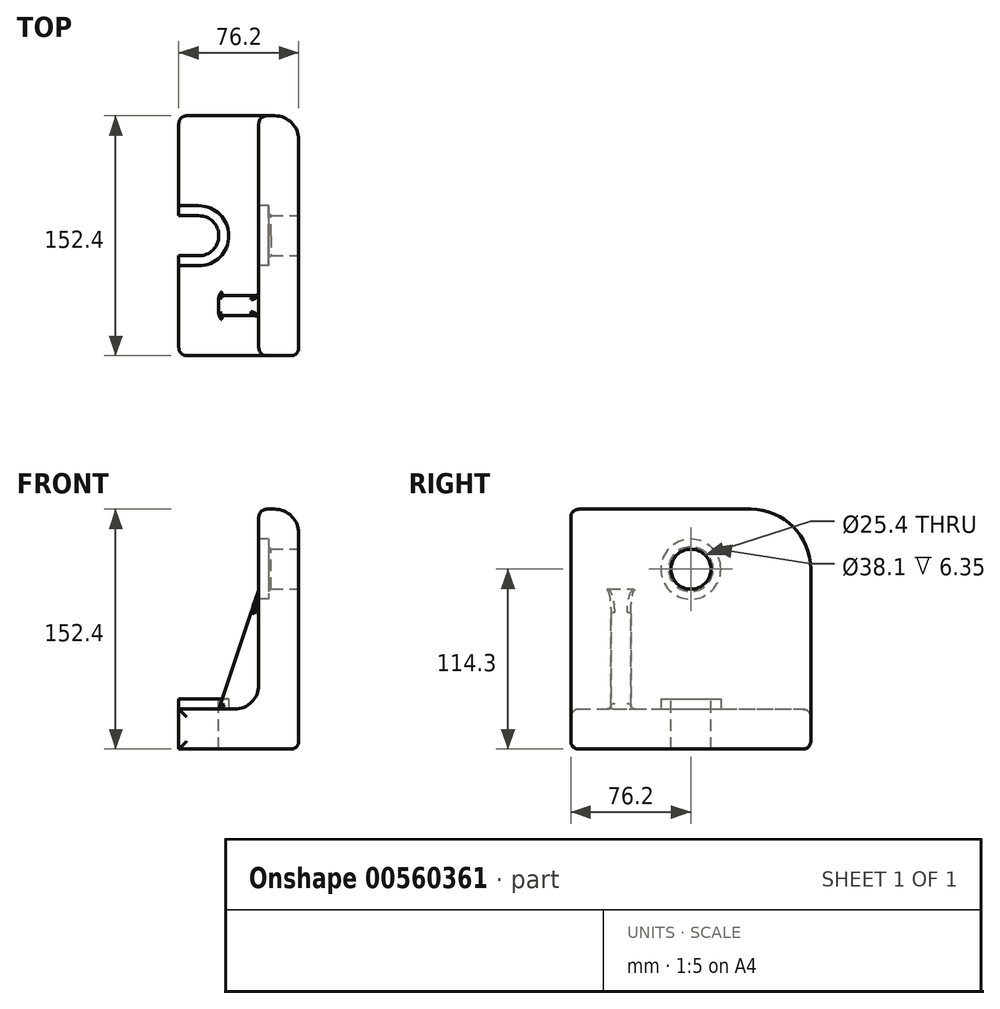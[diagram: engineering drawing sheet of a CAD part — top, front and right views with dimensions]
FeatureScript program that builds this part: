
annotation { "Feature Type Name" : "Feature", "Feature Type Description" : "" }
export const myFeature = defineFeature(function(context is Context, id is Id, definition is map)
    precondition{}
    {
        {
            var Q0;
            Q0=qCreatedBy(makeId("Front.planeOp"),FACE);
            var sketch = newSketch(context, id + "F0", { "sketchPlane" : qUnion([Q0])});
            skLineSegment(sketch, "E0.bottom", {"start": v(0, 0) * mm, "end": v(-76.2, 0) * mm});
            skLineSegment(sketch, "E0.top", {"start": v(-25.4, 25.4) * mm, "end": v(-76.2, 25.4) * mm});
            skLineSegment(sketch, "E0.left", {"start": v(0, 0) * mm, "end": v(0, 25.4) * mm});
            skLineSegment(sketch, "E0.right", {"start": v(-76.2, 0) * mm, "end": v(-76.2, 25.4) * mm});
            skLineSegment(sketch, "E1.bottom", {"start": v(0, 0) * mm, "end": v(-25.4, 0) * mm});
            skLineSegment(sketch, "E1.top", {"start": v(0, 152.4) * mm, "end": v(-25.4, 152.4) * mm});
            skLineSegment(sketch, "E1.left", {"start": v(0, 0) * mm, "end": v(0, 152.4) * mm});
            skLineSegment(sketch, "E1.right", {"start": v(-25.4, 25.4) * mm, "end": v(-25.4, 152.4) * mm});
            skSolve(sketch);
        }
        {
            var Q0;
            Q0 = qSketchRegion(id + "F0", true);
            extrude(context, id + "F1", {"entities" : qUnion([Q0]), "endBound" : BoundingType.SYMMETRIC, "depth" : 152.4 * mm, "offsetDistance" : 25.4 * mm});
        }
        {
            var Q0;
            Q0=makeQuery(id+"F1.opExtrude","SWEPT_FACE",FACE,{"disambiguationData":[OSD([sQuery(id+"F0.wireOp",EDGE,"E1.left")])]});
            var sketch = newSketch(context, id + "F2", { "sketchPlane" : qUnion([Q0])});
            skCircle(sketch, "E2", {"center": v(0, 114.3) * mm, "radius": 12.7 * mm});
            skSolve(sketch);
        }
        {
            var Q0;
            Q0=makeQuery(id+"F2.imprint","IMPRINT",FACE,{"disambiguationData":[TD([[makeQuery(id+"F2.imprint","IMPRINT",EDGE,{"derivedFrom":sQuery(id+"F2.wireOp",EDGE,"E2")}),1.0]])]});
            extrude(context, id + "F3", {"entities" : qUnion([Q0]), "operationType" : NewBodyOperationType.REMOVE, "endBound" : BoundingType.THROUGH_ALL, "oppositeDirection" : true, "depth" : 25.4 * mm, "offsetDistance" : 25.4 * mm});
        }
        {
            var Q0;
            Q0=makeQuery(id+"F1.opExtrude","SWEPT_FACE",FACE,{"disambiguationData":[OSD([sQuery(id+"F0.wireOp",EDGE,"E0.top")])]});
            var sketch = newSketch(context, id + "F4", { "sketchPlane" : qUnion([Q0])});
            skLineSegment(sketch, "E3", {"start": v(-76.2, 12.7) * mm, "end": v(-63.5, 12.7) * mm});
            skArc(sketch, "E4", {"start": v(-63.5, 12.7) * mm, "mid": v(-50.8, 0) * mm, "end": v(-63.5, -12.7) * mm});
            skLineSegment(sketch, "E5", {"start": v(-63.5, -12.7) * mm, "end": v(-76.2, -12.7) * mm});
            skLineSegment(sketch, "E6", {"start": v(-76.2, -12.7) * mm, "end": v(-76.2, 12.7) * mm});
            skSolve(sketch);
        }
        {
            var Q0;
            Q0 = qSketchRegion(id + "F4", true);
            extrude(context, id + "F5", {"entities" : qUnion([Q0]), "operationType" : NewBodyOperationType.REMOVE, "endBound" : BoundingType.THROUGH_ALL, "oppositeDirection" : true, "depth" : 25.4 * mm, "offsetDistance" : 25.4 * mm});
        }
        {
            var Q0;
            Q0=makeQuery(id+"F1.opExtrude","SWEPT_FACE",FACE,{"disambiguationData":[OSD([sQuery(id+"F0.wireOp",EDGE,"E1.right")])]});
            var sketch = newSketch(context, id + "F6", { "sketchPlane" : qUnion([Q0])});
            skLineSegment(sketch, "E7.0", {"start": v(-76.2, 25.4) * mm, "end": v(-76.2, 152.4) * mm});
            skLineSegment(sketch, "E7.1", {"start": v(76.2, 152.4) * mm, "end": v(-76.2, 152.4) * mm});
            skArc(sketch, "E8", {"start": v(-38.1, 152.4) * mm, "mid": v(-65.04, 141.24) * mm, "end": v(-76.2, 114.3) * mm});
            skSolve(sketch);
        }
        {
            var Q0;
            {var subQ3=sQuery(id+"F6.wireOp",EDGE,"E8");Q0=makeQuery(id+"F6.imprint","IMPRINT",FACE,{"disambiguationData":[TD([[makeQuery(id+"F6.imprint","IMPRINT",EDGE,{"derivedFrom":subQ3}),-1.0]])]});}
            extrude(context, id + "F7", {"entities" : qUnion([Q0]), "operationType" : NewBodyOperationType.REMOVE, "endBound" : BoundingType.THROUGH_ALL, "oppositeDirection" : true, "depth" : 25.4 * mm, "offsetDistance" : 25.4 * mm});
        }
        {
            var Q0;
            Q0=makeQuery(id+"F1.opExtrude","SWEPT_FACE",FACE,{"disambiguationData":[OSD([sQuery(id+"F0.wireOp",EDGE,"E1.right")])]});
            var sketch = newSketch(context, id + "F8", { "sketchPlane" : qUnion([Q0])});
            skCircle(sketch, "E9", {"center": v(0, 114.3) * mm, "radius": 19.05 * mm});
            skSolve(sketch);
        }
        {
            var Q0;
            Q0=makeQuery(id+"F8.imprint","IMPRINT",FACE,{"disambiguationData":[TD([[makeQuery(id+"F8.imprint","IMPRINT",EDGE,{"derivedFrom":makeQuery(id+"F3.boolean.opBoolean","INTERSECT",EDGE,{"derivedFrom":[makeQuery(id+"F1.opExtrude","SWEPT_FACE",FACE,{"disambiguationData":[OSD([sQuery(id+"F0.wireOp",EDGE,"E1.right")])]}),makeQuery(id+"F3.opExtrude","SWEPT_FACE",FACE,{"disambiguationData":[OSD([sQuery(id+"F2.wireOp",EDGE,"E2")])]})]})}),1.0]])]});
            var Q1;
            Q1=makeQuery(id+"F8.imprint","IMPRINT",FACE,{"disambiguationData":[TD([[makeQuery(id+"F8.imprint","IMPRINT",EDGE,{"derivedFrom":sQuery(id+"F8.wireOp",EDGE,"E9")}),1.0]])]});
            extrude(context, id + "F9", {"entities" : qUnion([Q0, Q1]), "operationType" : NewBodyOperationType.REMOVE, "oppositeDirection" : true, "depth" : 6.35 * mm, "offsetDistance" : 25.4 * mm});
        }
        {
            var Q0;
            Q0=qCreatedBy(makeId("Front.planeOp"),FACE);
            cPlane(context, id + "F10", {"entities" : qUnion([Q0]), "cplaneType" : CPlaneType.OFFSET, "offset" : 44.45 * mm, "width" : 152.4 * mm, "height" : 152.4 * mm});
        }
        {
            var Q0;
            Q0=qCreatedBy(id+"F10.planeOp",FACE);
            var sketch = newSketch(context, id + "F11", { "sketchPlane" : qUnion([Q0])});
            skLineSegment(sketch, "E10.0", {"start": v(-25.4, 25.4) * mm, "end": v(-76.2, 25.4) * mm});
            skLineSegment(sketch, "E10.1", {"start": v(-25.4, 25.4) * mm, "end": v(-25.4, 114.3) * mm});
            skLineSegment(sketch, "E11", {"start": v(-25.4, 101.6) * mm, "end": v(-50.8, 25.4) * mm});
            skLineSegment(sketch, "E12", {"start": v(-25.4, 101.6) * mm, "end": v(-25.4, 25.4) * mm});
            skLineSegment(sketch, "E13", {"start": v(-50.8, 25.4) * mm, "end": v(-25.4, 25.4) * mm});
            skLineSegment(sketch, "E14", {"start": v(-50.8, 25.4) * mm, "end": v(-76.2, 25.4) * mm});
            skSolve(sketch);
        }
        {
            var Q0;
            Q0=makeQuery(id+"F11.imprint","IMPRINT",FACE,{"disambiguationData":[TD([[makeQuery(id+"F11.imprint","IMPRINT",EDGE,{"derivedFrom":sQuery(id+"F11.wireOp",EDGE,"E11")}),1.0]])]});
            extrude(context, id + "F12", {"entities" : qUnion([Q0]), "operationType" : NewBodyOperationType.ADD, "endBound" : BoundingType.SYMMETRIC, "depth" : 12.7 * mm, "offsetDistance" : 25.4 * mm});
        }
        {
            var Q0;
            Q0=makeQuery(id+"F9.boolean.opBoolean","INTERSECT",EDGE,{"derivedFrom":[makeQuery(id+"F3.boolean.opBoolean","COPY",FACE,{"derivedFrom":makeQuery(id+"F3.opExtrude","SWEPT_FACE",FACE,{"disambiguationData":[OSD([sQuery(id+"F2.wireOp",EDGE,"E2")])]})}),makeQuery(id+"F9.opExtrude","CAP_FACE",FACE,{"disambiguationData":[OSD([sQuery(id+"F8.wireOp",EDGE,"E9")])],"isStart":false})]});
            var Q1;
            Q1=makeQuery(id+"F9.boolean.opBoolean","COPY",EDGE,{"derivedFrom":makeQuery(id+"F9.opExtrude","CAP_EDGE",EDGE,{"disambiguationData":[OSD([sQuery(id+"F8.wireOp",EDGE,"E9")])],"isStart":true})});
            chamfer(context, id + "F13", {"entities" : qUnion([Q0, Q1]), "width" : 1.52 * mm, "tangentPropagation" : true});
        }
        {
            var Q0;
            Q0=makeQuery(id+"F1.opExtrude","SWEPT_FACE",FACE,{"disambiguationData":[OSD([sQuery(id+"F0.wireOp",EDGE,"E0.top")])]});
            var sketch = newSketch(context, id + "F14", { "sketchPlane" : qUnion([Q0])});
            skLineSegment(sketch, "E15.0", {"start": v(-76.2, 12.7) * mm, "end": v(-76.2, 76.2) * mm});
            skLineSegment(sketch, "E15.1", {"start": v(-76.2, 12.7) * mm, "end": v(-63.5, 12.7) * mm});
            skArc(sketch, "E15.2", {"start": v(-63.5, 12.7) * mm, "mid": v(-50.8, 0) * mm, "end": v(-63.5, -12.7) * mm});
            skLineSegment(sketch, "E15.3", {"start": v(-63.5, -12.7) * mm, "end": v(-76.2, -12.7) * mm});
            skLineSegment(sketch, "E15.4", {"start": v(-76.2, -76.2) * mm, "end": v(-76.2, -12.7) * mm});
            skLineSegment(sketch, "E16.0", {"start": v(-76.2, 19.05) * mm, "end": v(-63.5, 19.05) * mm});
            skArc(sketch, "E17.0", {"start": v(-63.5, 19.05) * mm, "mid": v(-44.45, 0) * mm, "end": v(-63.5, -19.05) * mm});
            skLineSegment(sketch, "E18.0", {"start": v(-63.5, -19.05) * mm, "end": v(-76.2, -19.05) * mm});
            skSolve(sketch);
        }
        {
            var Q0;
            {var subQ1=sQuery(id+"F14.wireOp",EDGE,"E15.1");Q0=makeQuery(id+"F14.imprint","IMPRINT",FACE,{"disambiguationData":[TD([[makeQuery(id+"F14.imprint","IMPRINT",EDGE,{"derivedFrom":subQ1}),1.0]])]});}
            extrude(context, id + "F15", {"entities" : qUnion([Q0]), "operationType" : NewBodyOperationType.ADD, "depth" : 6.35 * mm, "offsetDistance" : 25.4 * mm});
        }
        {
            var Q0;
            Q0=makeQuery(id+"F1.opExtrude","SWEPT_EDGE",EDGE,{"disambiguationData":[OSD([sQuery(id+"F0.wireOp",EDGE,"E1.bottom"),sQuery(id+"F0.wireOp",EDGE,"E1.left")])]});
            var Q1;
            {var subQ0=sQuery(id+"F0.wireOp",EDGE,"E1.right");var subQ1=sQuery(id+"F0.wireOp",EDGE,"E0.top");var subQ5=sQuery(id+"F11.wireOp",EDGE,"E13");var subQ6=sQuery(id+"F11.wireOp",EDGE,"E12");var subQ7=sQuery(id+"F11.wireOp",EDGE,"E11");Q1=makeQuery(id+"FHcutw4A6m2gUYd_1.1.F12.boolean.opBoolean","SPLIT",EDGE,{"disambiguationData":[TD([makeQuery(id+"FHcutw4A6m2gUYd_1.1.F12.opExtrude","CAP_FACE",FACE,{"disambiguationData":[OSD([subQ7,subQ6,subQ5])],"isStart":false})])],"derivedFrom":makeQuery(id+"F12.boolean.opBoolean","SPLIT",EDGE,{"disambiguationData":[TD([makeQuery(id+"F12.opExtrude","CAP_FACE",FACE,{"disambiguationData":[OSD([subQ7,subQ6,subQ5])],"isStart":true})])],"derivedFrom":makeQuery(id+"F1.opExtrude","SWEPT_EDGE",EDGE,{"disambiguationData":[OSD([subQ1,subQ0])]})})});}
            var Q2;
            {var subQ0=sQuery(id+"F0.wireOp",EDGE,"E0.top");var subQ2=sQuery(id+"F0.wireOp",EDGE,"E1.right");var subQ4=sQuery(id+"F11.wireOp",EDGE,"E13");var subQ5=sQuery(id+"F11.wireOp",EDGE,"E12");var subQ6=sQuery(id+"F11.wireOp",EDGE,"E11");var subQ7=makeQuery(id+"F12.opExtrude","CAP_FACE",FACE,{"disambiguationData":[OSD([subQ6,subQ5,subQ4])],"isStart":true});Q2=makeQuery(id+"FHcutw4A6m2gUYd_1.1.F12.boolean.opBoolean","SPLIT",EDGE,{"disambiguationData":[TD([subQ7])],"derivedFrom":makeQuery(id+"F12.boolean.opBoolean","SPLIT",EDGE,{"disambiguationData":[TD([subQ7])],"derivedFrom":makeQuery(id+"F1.opExtrude","SWEPT_EDGE",EDGE,{"disambiguationData":[OSD([subQ0,subQ2])]})})});}
            var Q3;
            {var subQ0=sQuery(id+"F0.wireOp",EDGE,"E1.right");var subQ1=sQuery(id+"F0.wireOp",EDGE,"E0.top");Q3=makeQuery(id+"F12.boolean.opBoolean","SPLIT",EDGE,{"disambiguationData":[TD([makeQuery(id+"F12.opExtrude","CAP_FACE",FACE,{"disambiguationData":[OSD([sQuery(id+"F11.wireOp",EDGE,"E11"),sQuery(id+"F11.wireOp",EDGE,"E12"),sQuery(id+"F11.wireOp",EDGE,"E13")])],"isStart":false})])],"derivedFrom":makeQuery(id+"F1.opExtrude","SWEPT_EDGE",EDGE,{"disambiguationData":[OSD([subQ1,subQ0])]})});}
            fillet(context, id + "F16", {"entities" : qUnion([Q0, Q1, Q2, Q3]), "radius" : 15.24 * mm, "tangentPropagation" : true, "allowEdgeOverflow" : false});
        }
        {
            var Q0;
            Q0=makeQuery(id+"F1.opExtrude","CAP_EDGE",EDGE,{"disambiguationData":[OSD([sQuery(id+"F0.wireOp",EDGE,"E0.top")])],"isStart":false});
            var Q1;
            Q1=makeQuery(id+"F1.opExtrude","CAP_EDGE",EDGE,{"disambiguationData":[OSD([sQuery(id+"F0.wireOp",EDGE,"E1.right")])],"isStart":false});
            var Q2;
            Q2=makeQuery(id+"F1.opExtrude","CAP_EDGE",EDGE,{"disambiguationData":[OSD([sQuery(id+"F0.wireOp",EDGE,"E0.top")])],"isStart":true});
            var Q3;
            Q3=makeQuery(id+"F1.opExtrude","CAP_FACE",FACE,{"disambiguationData":[OSD([sQuery(id+"F0.wireOp",EDGE,"E0.bottom"),sQuery(id+"F0.wireOp",EDGE,"E0.top"),sQuery(id+"F0.wireOp",EDGE,"E0.right"),sQuery(id+"F0.wireOp",EDGE,"E1.bottom"),sQuery(id+"F0.wireOp",EDGE,"E1.top"),sQuery(id+"F0.wireOp",EDGE,"E1.left"),sQuery(id+"F0.wireOp",EDGE,"E1.right")])],"isStart":true});
            var Q4;
            Q4=makeQuery(id+"F1.opExtrude","CAP_FACE",FACE,{"disambiguationData":[OSD([sQuery(id+"F0.wireOp",EDGE,"E0.bottom"),sQuery(id+"F0.wireOp",EDGE,"E0.top"),sQuery(id+"F0.wireOp",EDGE,"E0.right"),sQuery(id+"F0.wireOp",EDGE,"E1.bottom"),sQuery(id+"F0.wireOp",EDGE,"E1.top"),sQuery(id+"F0.wireOp",EDGE,"E1.left"),sQuery(id+"F0.wireOp",EDGE,"E1.right")])],"isStart":false});
            fillet(context, id + "F17", {"entities" : qUnion([Q0, Q1, Q2, Q3, Q4]), "radius" : 5.08 * mm, "tangentPropagation" : true, "allowEdgeOverflow" : false});
        }
        {
            var Q0;
            {var subQ0=makeQuery(id+"F12.opExtrude","CAP_FACE",FACE,{"disambiguationData":[OSD([sQuery(id+"F11.wireOp",EDGE,"E11"),sQuery(id+"F11.wireOp",EDGE,"E12"),sQuery(id+"F11.wireOp",EDGE,"E13")])],"isStart":false});var subQ1=sQuery(id+"F0.wireOp",EDGE,"E1.right");var subQ2=sQuery(id+"F0.wireOp",EDGE,"E0.top");Q0=makeQuery(id+"F16.opFillet","BLEND_EDGE",EDGE,{"blendedFrom":[makeQuery(id+"F12.boolean.opBoolean","SPLIT",EDGE,{"disambiguationData":[TD([subQ0])],"derivedFrom":makeQuery(id+"F1.opExtrude","SWEPT_EDGE",EDGE,{"disambiguationData":[OSD([subQ2,subQ1])]})}),subQ0],"blendedInto":[subQ0]});}
            var Q1;
            Q1=makeQuery(id+"F12.opExtrude","SWEPT_EDGE",EDGE,{"disambiguationData":[OSD([sQuery(id+"F11.wireOp",EDGE,"E11"),sQuery(id+"F11.wireOp",EDGE,"E13")])]});
            var Q2;
            {var subQ0=sQuery(id+"F11.wireOp",EDGE,"E13");var subQ1=sQuery(id+"F11.wireOp",EDGE,"E12");var subQ2=sQuery(id+"F11.wireOp",EDGE,"E11");var subQ3=makeQuery(id+"FHcutw4A6m2gUYd_1.1.F12.opExtrude","CAP_FACE",FACE,{"disambiguationData":[OSD([subQ2,subQ1,subQ0])],"isStart":true});var subQ4=sQuery(id+"F0.wireOp",EDGE,"E0.top");var subQ6=sQuery(id+"F0.wireOp",EDGE,"E1.right");var subQ8=makeQuery(id+"F12.opExtrude","CAP_FACE",FACE,{"disambiguationData":[OSD([subQ2,subQ1,subQ0])],"isStart":true});Q2=makeQuery(id+"F16.opFillet","BLEND_EDGE",EDGE,{"blendedFrom":[makeQuery(id+"FHcutw4A6m2gUYd_1.1.F12.boolean.opBoolean","SPLIT",EDGE,{"disambiguationData":[TD([subQ8])],"derivedFrom":makeQuery(id+"F12.boolean.opBoolean","SPLIT",EDGE,{"disambiguationData":[TD([subQ8])],"derivedFrom":makeQuery(id+"F1.opExtrude","SWEPT_EDGE",EDGE,{"disambiguationData":[OSD([subQ4,subQ6])]})})}),subQ3],"blendedInto":[subQ3]});}
            var Q3;
            Q3=makeQuery(id+"FHcutw4A6m2gUYd_1.1.F12.opExtrude","SWEPT_EDGE",EDGE,{"disambiguationData":[OSD([sQuery(id+"F11.wireOp",EDGE,"E11"),sQuery(id+"F11.wireOp",EDGE,"E13")])]});
            var Q4;
            {var subQ0=sQuery(id+"F11.wireOp",EDGE,"E13");var subQ1=sQuery(id+"F11.wireOp",EDGE,"E12");var subQ2=sQuery(id+"F11.wireOp",EDGE,"E11");var subQ3=makeQuery(id+"F12.opExtrude","CAP_FACE",FACE,{"disambiguationData":[OSD([subQ2,subQ1,subQ0])],"isStart":true});var subQ4=sQuery(id+"F0.wireOp",EDGE,"E0.top");var subQ6=sQuery(id+"F0.wireOp",EDGE,"E1.right");Q4=makeQuery(id+"F16.opFillet","BLEND_EDGE",EDGE,{"blendedFrom":[makeQuery(id+"FHcutw4A6m2gUYd_1.1.F12.boolean.opBoolean","SPLIT",EDGE,{"disambiguationData":[TD([subQ3])],"derivedFrom":makeQuery(id+"F12.boolean.opBoolean","SPLIT",EDGE,{"disambiguationData":[TD([subQ3])],"derivedFrom":makeQuery(id+"F1.opExtrude","SWEPT_EDGE",EDGE,{"disambiguationData":[OSD([subQ4,subQ6])]})})}),subQ3],"blendedInto":[subQ3]});}
            var Q5;
            {var subQ0=sQuery(id+"F11.wireOp",EDGE,"E13");var subQ1=sQuery(id+"F11.wireOp",EDGE,"E12");var subQ2=sQuery(id+"F11.wireOp",EDGE,"E11");var subQ3=makeQuery(id+"FHcutw4A6m2gUYd_1.1.F12.opExtrude","CAP_FACE",FACE,{"disambiguationData":[OSD([subQ2,subQ1,subQ0])],"isStart":false});var subQ4=sQuery(id+"F0.wireOp",EDGE,"E1.right");var subQ5=sQuery(id+"F0.wireOp",EDGE,"E0.top");Q5=makeQuery(id+"F16.opFillet","BLEND_EDGE",EDGE,{"blendedFrom":[makeQuery(id+"FHcutw4A6m2gUYd_1.1.F12.boolean.opBoolean","SPLIT",EDGE,{"disambiguationData":[TD([subQ3])],"derivedFrom":makeQuery(id+"F12.boolean.opBoolean","SPLIT",EDGE,{"disambiguationData":[TD([makeQuery(id+"F12.opExtrude","CAP_FACE",FACE,{"disambiguationData":[OSD([subQ2,subQ1,subQ0])],"isStart":true})])],"derivedFrom":makeQuery(id+"F1.opExtrude","SWEPT_EDGE",EDGE,{"disambiguationData":[OSD([subQ5,subQ4])]})})}),subQ3],"blendedInto":[subQ3]});}
            var Q6;
            Q6=makeQuery(id+"FHcutw4A6m2gUYd_1.1.F12.opExtrude","SWEPT_EDGE",EDGE,{"disambiguationData":[OSD([sQuery(id+"F11.wireOp",EDGE,"E11"),sQuery(id+"F11.wireOp",EDGE,"E12")])]});
            var Q7;
            Q7=makeQuery(id+"F12.opExtrude","SWEPT_EDGE",EDGE,{"disambiguationData":[OSD([sQuery(id+"F11.wireOp",EDGE,"E11"),sQuery(id+"F11.wireOp",EDGE,"E12")])]});
            fillet(context, id + "F18", {"entities" : qUnion([Q0, Q1, Q2, Q3, Q4, Q5, Q6, Q7]), "radius" : 2.54 * mm, "tangentPropagation" : true, "allowEdgeOverflow" : false});
        }
        {
            var Q0;
            Q0=makeQuery(id+"FHcutw4A6m2gUYd_1.1.F12.opExtrude","CAP_EDGE",EDGE,{"disambiguationData":[OSD([sQuery(id+"F11.wireOp",EDGE,"E11")])],"isStart":true});
            var Q1;
            Q1=makeQuery(id+"FHcutw4A6m2gUYd_1.1.F12.opExtrude","CAP_EDGE",EDGE,{"disambiguationData":[OSD([sQuery(id+"F11.wireOp",EDGE,"E11")])],"isStart":false});
            var Q2;
            Q2=makeQuery(id+"F12.opExtrude","CAP_EDGE",EDGE,{"disambiguationData":[OSD([sQuery(id+"F11.wireOp",EDGE,"E11")])],"isStart":true});
            var Q3;
            Q3=makeQuery(id+"F12.opExtrude","CAP_EDGE",EDGE,{"disambiguationData":[OSD([sQuery(id+"F11.wireOp",EDGE,"E11")])],"isStart":false});
            fillet(context, id + "F19", {"entities" : qUnion([Q0, Q1, Q2, Q3]), "radius" : 2.54 * mm, "tangentPropagation" : true, "allowEdgeOverflow" : false});
        }
    });
